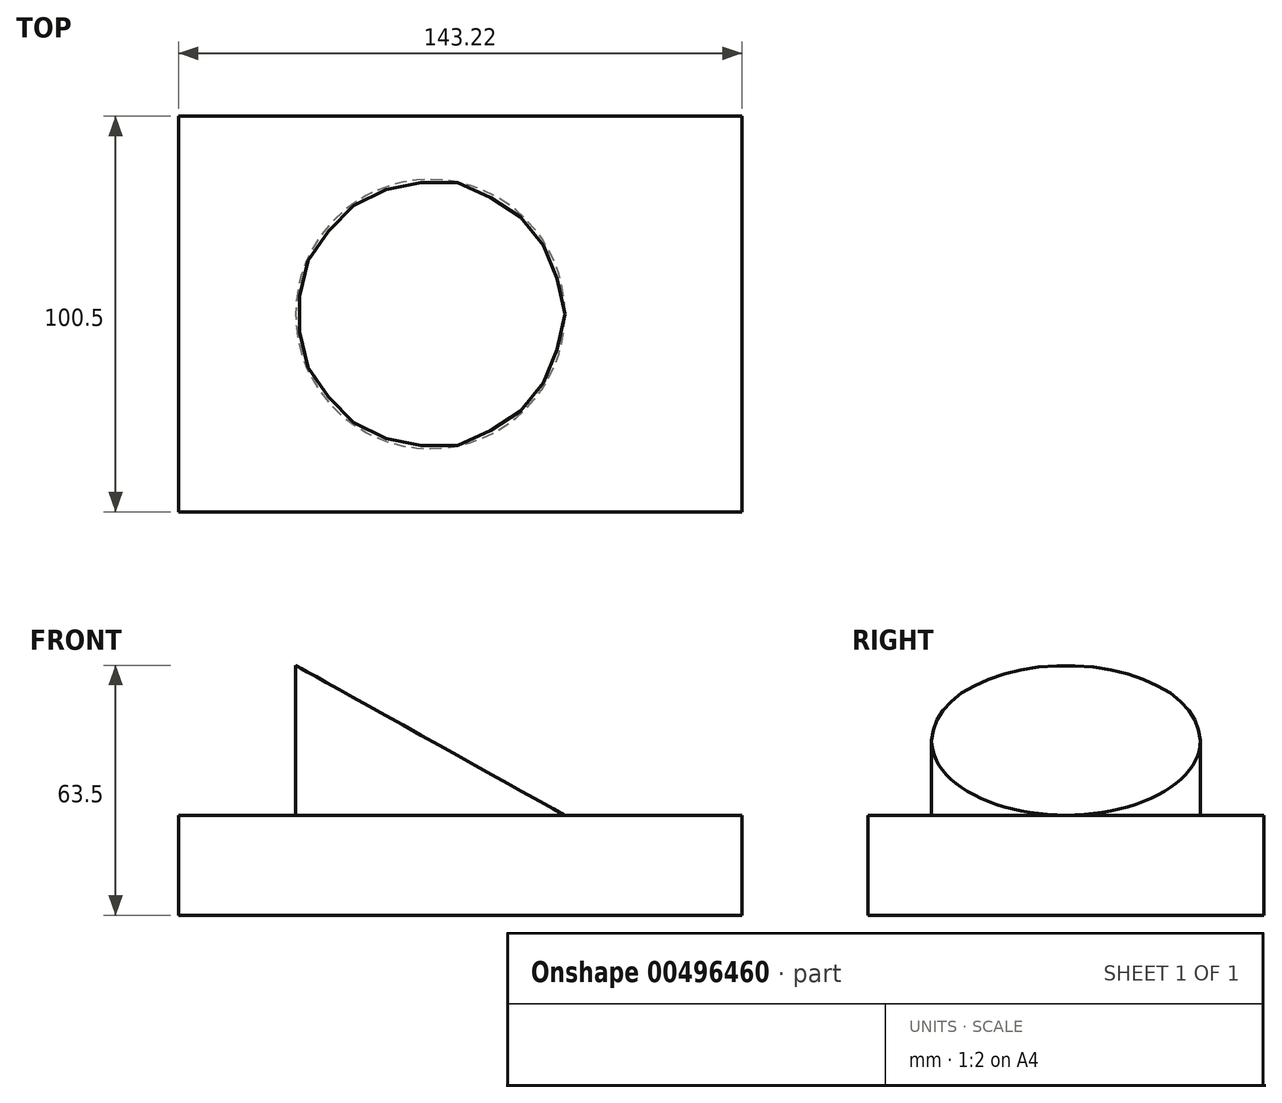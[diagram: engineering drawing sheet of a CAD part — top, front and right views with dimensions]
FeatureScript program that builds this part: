
annotation { "Feature Type Name" : "Feature", "Feature Type Description" : "" }
export const myFeature = defineFeature(function(context is Context, id is Id, definition is map)
    precondition{}
    {
        {
            var Q0;
            Q0=qCreatedBy(makeId("Top.planeOp"),FACE);
            var sketch = newSketch(context, id + "F0", { "sketchPlane" : qUnion([Q0])});
            skLineSegment(sketch, "E0.bottom", {"start": v(71.61, -50.25) * mm, "end": v(-71.61, -50.25) * mm});
            skLineSegment(sketch, "E0.top", {"start": v(71.61, 50.25) * mm, "end": v(-71.61, 50.25) * mm});
            skLineSegment(sketch, "E0.left", {"start": v(71.61, -50.25) * mm, "end": v(71.61, 50.25) * mm});
            skLineSegment(sketch, "E0.right", {"start": v(-71.61, -50.25) * mm, "end": v(-71.61, 50.25) * mm});
            skPoint(sketch, "E0.middle", {"position": v(0, 0) * mm});
            skSolve(sketch);
        }
        {
            var Q0;
            Q0 = qSketchRegion(id + "F0", true);
            extrude(context, id + "F1", {"entities" : qUnion([Q0]), "depth" : 25.4 * mm});
        }
        {
            var Q0;
            Q0=makeQuery(id+"F1.opExtrude","CAP_FACE",FACE,{"disambiguationData":[OSD([sQuery(id+"F0.wireOp",EDGE,"E0.bottom"),sQuery(id+"F0.wireOp",EDGE,"E0.top"),sQuery(id+"F0.wireOp",EDGE,"E0.left"),sQuery(id+"F0.wireOp",EDGE,"E0.right")])],"isStart":false});
            var sketch = newSketch(context, id + "F2", { "sketchPlane" : qUnion([Q0])});
            skCircle(sketch, "E1", {"center": v(-7.64, 0) * mm, "radius": 34.2 * mm});
            skSolve(sketch);
        }
        {
            var Q0;
            Q0=makeQuery(id+"F2.imprint","IMPRINT",FACE,{"disambiguationData":[TD([[makeQuery(id+"F2.imprint","IMPRINT",EDGE,{"derivedFrom":sQuery(id+"F2.wireOp",EDGE,"E1")}),1.0]])]});
            extrude(context, id + "F3", {"entities" : qUnion([Q0]), "operationType" : NewBodyOperationType.ADD, "depth" : 38.1 * mm});
        }
        {
            var Q0;
            Q0=makeQuery(id+"F1.opExtrude","SWEPT_FACE",FACE,{"disambiguationData":[OSD([sQuery(id+"F0.wireOp",EDGE,"E0.bottom")])]});
            var sketch = newSketch(context, id + "F4", { "sketchPlane" : qUnion([Q0])});
            skLineSegment(sketch, "E2", {"start": v(-41.84, 25.4) * mm, "end": v(-41.84, 63.5) * mm});
            skLineSegment(sketch, "E3", {"start": v(26.57, 63.5) * mm, "end": v(26.57, 25.4) * mm});
            skLineSegment(sketch, "E4", {"start": v(-41.84, 63.5) * mm, "end": v(26.57, 25.4) * mm});
            skLineSegment(sketch, "E5", {"start": v(-41.84, 63.5) * mm, "end": v(26.57, 63.5) * mm});
            skSolve(sketch);
        }
        {
            var Q0;
            Q0=makeQuery(id+"F4.imprint","IMPRINT",FACE,{"disambiguationData":[TD([[makeQuery(id+"F4.imprint","IMPRINT",EDGE,{"derivedFrom":sQuery(id+"F4.wireOp",EDGE,"E3")}),-1.0]])]});
            extrude(context, id + "F5", {"entities" : qUnion([Q0]), "operationType" : NewBodyOperationType.REMOVE, "oppositeDirection" : true, "depth" : 127 * mm});
        }
    });
